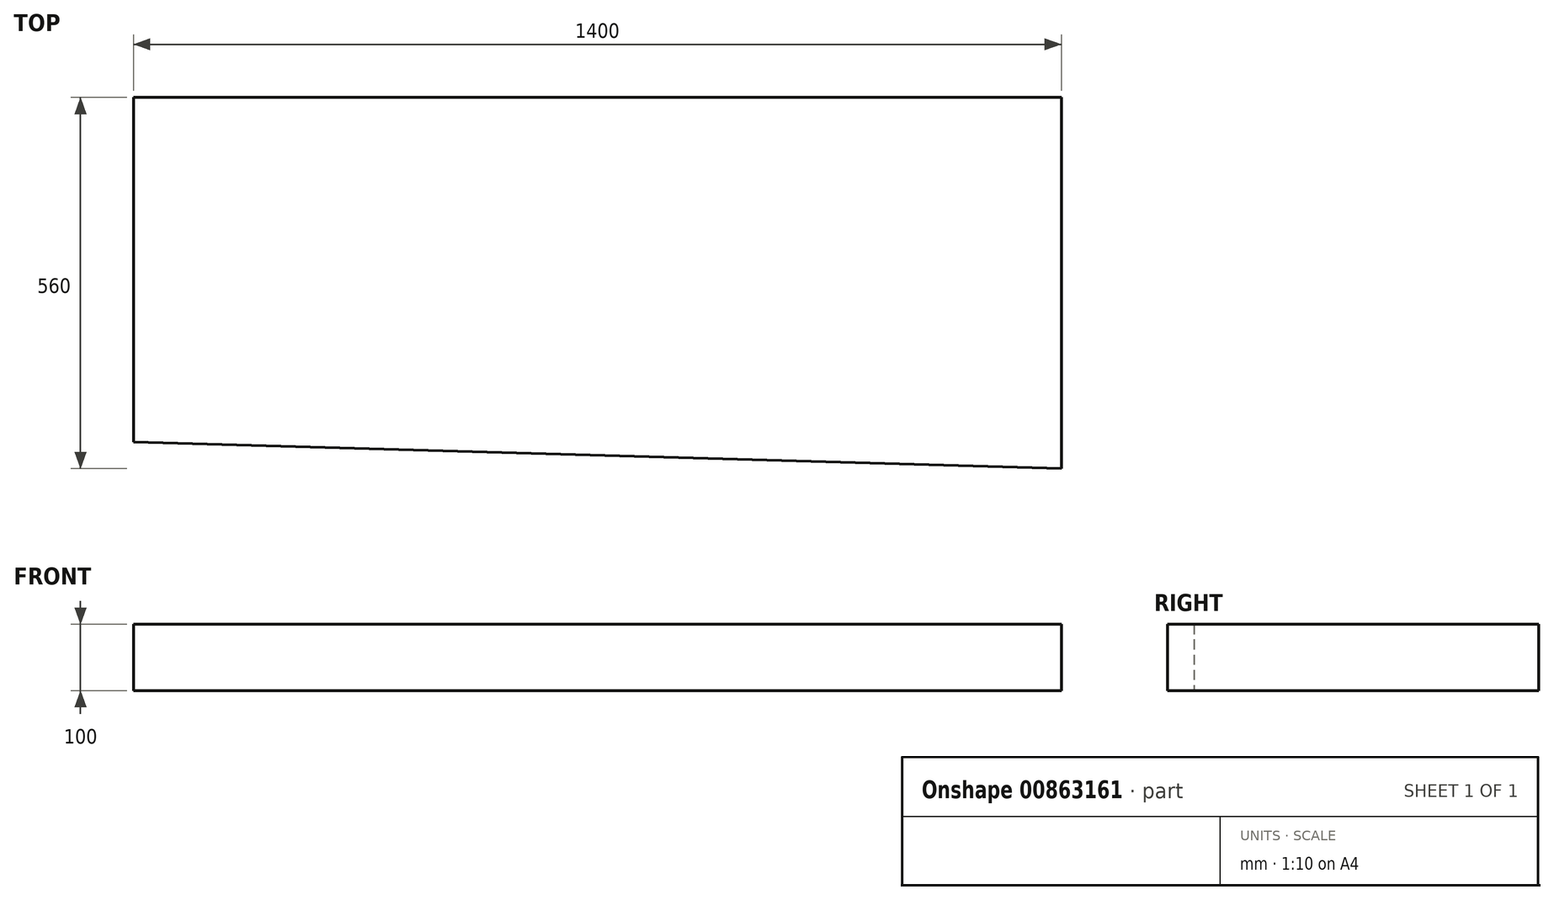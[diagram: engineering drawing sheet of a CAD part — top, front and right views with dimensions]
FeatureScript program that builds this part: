
annotation { "Feature Type Name" : "Feature", "Feature Type Description" : "" }
export const myFeature = defineFeature(function(context is Context, id is Id, definition is map)
    precondition{}
    {
        {
            var Q0;
            Q0=qCreatedBy(makeId("Top.planeOp"),FACE);
            var sketch = newSketch(context, id + "F0", { "sketchPlane" : qUnion([Q0])});
            skLineSegment(sketch, "E0", {"start": v(0, 0) * mm, "end": v(0, 520) * mm});
            skLineSegment(sketch, "E1", {"start": v(0, 520) * mm, "end": v(1400, 520) * mm});
            skLineSegment(sketch, "E2", {"start": v(1400, 520) * mm, "end": v(1400, -40) * mm});
            skLineSegment(sketch, "E3", {"start": v(1400, -40) * mm, "end": v(0, 0) * mm});
            skSolve(sketch);
        }
        {
            var Q0;
            Q0=makeQuery(id+"F0.imprint","IMPRINT",FACE,{"disambiguationData":[TD([[makeQuery(id+"F0.imprint","IMPRINT",EDGE,{"derivedFrom":sQuery(id+"F0.wireOp",EDGE,"E0")}),-1.0]])]});
            extrude(context, id + "F1", {"entities" : qUnion([Q0]), "depth" : 100 * mm, "offsetDistance" : 25 * mm});
        }
    });
